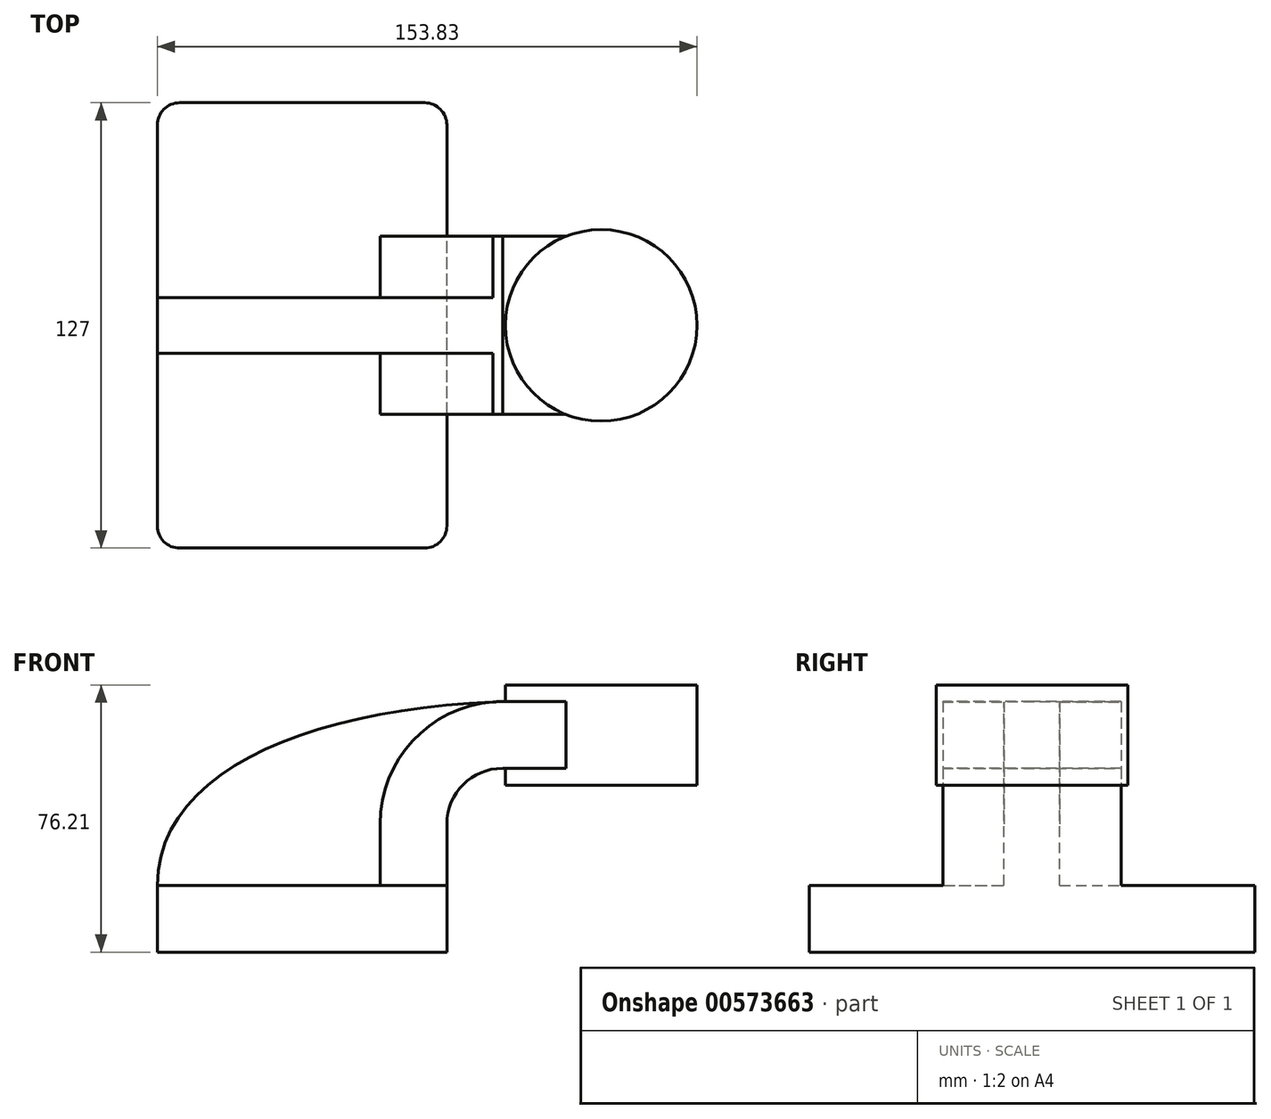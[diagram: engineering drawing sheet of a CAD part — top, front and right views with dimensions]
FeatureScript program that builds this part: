
annotation { "Feature Type Name" : "Feature", "Feature Type Description" : "" }
export const myFeature = defineFeature(function(context is Context, id is Id, definition is map)
    precondition{}
    {
        {
            var Q0;
            Q0=qCreatedBy(makeId("Front.planeOp"),FACE);
            var sketch = newSketch(context, id + "F0", { "sketchPlane" : qUnion([Q0])});
            skLineSegment(sketch, "E0.bottom", {"start": v(-41.28, 9.52) * mm, "end": v(41.28, 9.53) * mm});
            skLineSegment(sketch, "E0.top", {"start": v(-41.28, -9.53) * mm, "end": v(41.28, -9.53) * mm});
            skLineSegment(sketch, "E0.left", {"start": v(-41.28, 9.52) * mm, "end": v(-41.28, -9.53) * mm});
            skLineSegment(sketch, "E0.right", {"start": v(41.28, 9.53) * mm, "end": v(41.28, -9.52) * mm});
            skPoint(sketch, "E0.middle", {"position": v(0, 0) * mm});
            skLineSegment(sketch, "E1.bottom", {"start": v(61.75, 66.67) * mm, "end": v(112.55, 66.67) * mm});
            skLineSegment(sketch, "E1.top", {"start": v(61.75, 38.1) * mm, "end": v(112.55, 38.1) * mm});
            skLineSegment(sketch, "E1.left", {"start": v(61.75, 66.67) * mm, "end": v(61.75, 38.1) * mm});
            skLineSegment(sketch, "E1.right", {"start": v(112.55, 66.67) * mm, "end": v(112.55, 38.1) * mm});
            skPoint(sketch, "E1.middle", {"position": v(87.15, 52.39) * mm});
            skLineSegment(sketch, "E2", {"start": v(41.27, 9.53) * mm, "end": v(41.27, 27) * mm});
            skArc(sketch, "E3", {"start": v(41.27, 27) * mm, "mid": v(45.92, 38.23) * mm, "end": v(57.15, 42.88) * mm});
            skLineSegment(sketch, "E4", {"start": v(57.15, 42.88) * mm, "end": v(85.24, 42.88) * mm});
            skLineSegment(sketch, "E5.0", {"start": v(57.15, 61.93) * mm, "end": v(85.24, 61.93) * mm});
            skArc(sketch, "E5.1", {"start": v(22.22, 27) * mm, "mid": v(32.45, 51.7) * mm, "end": v(57.15, 61.93) * mm});
            skLineSegment(sketch, "E5.2", {"start": v(22.22, 9.53) * mm, "end": v(22.22, 27) * mm});
            skLineSegment(sketch, "E6", {"start": v(85.24, 38.1) * mm, "end": v(85.24, 66.67) * mm});
            skFitSpline(sketch, "E7", {"points": [v(-41.28, 9.52) * mm, v(57.15, 61.93) * mm], "startDerivative": vector(0.88, 100.7) * mm, "endDerivative": vector(159.08, 5.44) * mm});
            skSolve(sketch);
        }
        {
            var Q0;
            Q0=makeQuery(id+"F0.imprint","IMPRINT",FACE,{"disambiguationData":[TD([[makeQuery(id+"F0.imprint","IMPRINT",EDGE,{"derivedFrom":sQuery(id+"F0.wireOp",EDGE,"E0.top")}),1.0]])]});
            extrude(context, id + "F1", {"entities" : qUnion([Q0]), "endBound" : BoundingType.SYMMETRIC, "depth" : 127 * mm, "offsetDistance" : 25.4 * mm});
        }
        {
            var Q0;
            {var subQ1=sQuery(id+"F0.wireOp",EDGE,"E2");Q0=makeQuery(id+"F0.imprint","IMPRINT",FACE,{"disambiguationData":[TD([[makeQuery(id+"F0.imprint","IMPRINT",EDGE,{"derivedFrom":subQ1}),1.0]])]});}
            var Q1;
            {var subQ0=sQuery(id+"F0.wireOp",EDGE,"E5.0");var subQ1=sQuery(id+"F0.wireOp",EDGE,"E1.left");var subQ2=makeQuery(id+"F0.imprint","INTERSECT",VERTEX,{"derivedFrom":[subQ1,subQ0]});Q1=makeQuery(id+"F0.imprint","IMPRINT",FACE,{"disambiguationData":[TD([[makeQuery(id+"F0.imprint","IMPRINT",EDGE,{"disambiguationData":[TD([[subQ2,-1.0]])],"derivedFrom":subQ1}),1.0]])]});}
            extrude(context, id + "F2", {"entities" : qUnion([Q0, Q1]), "operationType" : NewBodyOperationType.ADD, "endBound" : BoundingType.SYMMETRIC, "depth" : 50.8 * mm, "offsetDistance" : 25.4 * mm});
        }
        {
            var Q0;
            {var subQ3=sQuery(id+"F0.wireOp",EDGE,"E5.2");Q0=makeQuery(id+"F0.imprint","IMPRINT",FACE,{"disambiguationData":[TD([[makeQuery(id+"F0.imprint","IMPRINT",EDGE,{"derivedFrom":subQ3}),1.0]])]});}
            extrude(context, id + "F3", {"entities" : qUnion([Q0]), "operationType" : NewBodyOperationType.ADD, "endBound" : BoundingType.SYMMETRIC, "depth" : 15.88 * mm, "offsetDistance" : 25.4 * mm});
        }
        {
            var Q0;
            {var subQ4=sQuery(id+"F0.wireOp",EDGE,"E1.right");Q0=makeQuery(id+"F0.imprint","IMPRINT",FACE,{"disambiguationData":[TD([[makeQuery(id+"F0.imprint","IMPRINT",EDGE,{"derivedFrom":subQ4}),-1.0]])]});}
            var Q1;
            Q1=sQuery(id+"F0.wireOp",EDGE,"E6");
            revolve(context, id + "F4", {"operationType" : NewBodyOperationType.ADD, "entities" : qUnion([Q0]), "axis" : qUnion([Q1]), "revolveType" : RevolveType.FULL});
        }
        {
            var Q0;
            Q0=makeQuery(id+"F1.opExtrude","CAP_EDGE",EDGE,{"disambiguationData":[OSD([sQuery(id+"F0.wireOp",EDGE,"E0.left")])],"isStart":false});
            var Q1;
            Q1=makeQuery(id+"F1.opExtrude","CAP_EDGE",EDGE,{"disambiguationData":[OSD([sQuery(id+"F0.wireOp",EDGE,"E0.right")])],"isStart":false});
            var Q2;
            Q2=makeQuery(id+"F1.opExtrude","CAP_EDGE",EDGE,{"disambiguationData":[OSD([sQuery(id+"F0.wireOp",EDGE,"E0.left")])],"isStart":true});
            var Q3;
            Q3=makeQuery(id+"F1.opExtrude","CAP_EDGE",EDGE,{"disambiguationData":[OSD([sQuery(id+"F0.wireOp",EDGE,"E0.right")])],"isStart":true});
            fillet(context, id + "F5", {"entities" : qUnion([Q0, Q1, Q2, Q3]), "radius" : 6.35 * mm, "tangentPropagation" : true, "allowEdgeOverflow" : false});
        }
    });
